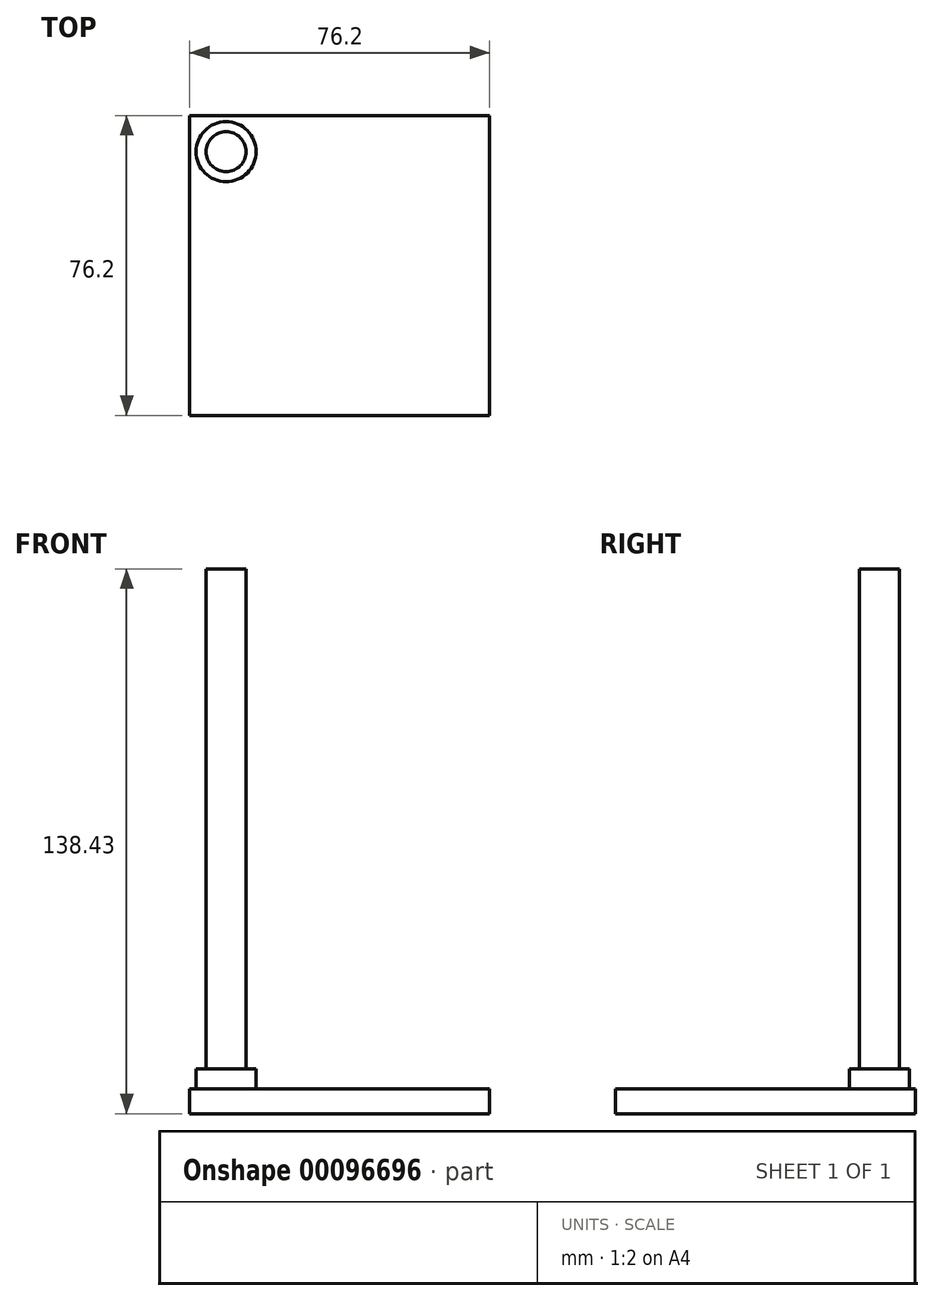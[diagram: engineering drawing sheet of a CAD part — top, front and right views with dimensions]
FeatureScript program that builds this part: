
annotation { "Feature Type Name" : "Feature", "Feature Type Description" : "" }
export const myFeature = defineFeature(function(context is Context, id is Id, definition is map)
    precondition{}
    {
        {
            var Q0;
            Q0=qCreatedBy(makeId("Top.planeOp"),FACE);
            var sketch = newSketch(context, id + "F0", { "sketchPlane" : qUnion([Q0])});
            skLineSegment(sketch, "E0.bottom", {"start": v(20.65, 3.83) * mm, "end": v(-55.55, 3.83) * mm});
            skLineSegment(sketch, "E0.top", {"start": v(20.65, -72.37) * mm, "end": v(-55.55, -72.37) * mm});
            skLineSegment(sketch, "E0.left", {"start": v(20.65, 3.83) * mm, "end": v(20.65, -72.37) * mm});
            skLineSegment(sketch, "E0.right", {"start": v(-55.55, 3.83) * mm, "end": v(-55.55, -72.37) * mm});
            skPoint(sketch, "E0.middle", {"position": v(-17.45, -34.27) * mm});
            skLineSegment(sketch, "E1", {"start": v(-55.55, 3.83) * mm, "end": v(-17.45, -34.27) * mm, "construction": true});
            skCircle(sketch, "E2", {"center": v(-46.33, -5.4) * mm, "radius": 5.08 * mm});
            skCircle(sketch, "E3", {"center": v(-46.33, -5.4) * mm, "radius": 7.62 * mm});
            skSolve(sketch);
        }
        {
            var Q0;
            Q0=makeQuery(id+"F0.imprint","IMPRINT",FACE,{"disambiguationData":[TD([[makeQuery(id+"F0.imprint","IMPRINT",EDGE,{"derivedFrom":sQuery(id+"F0.wireOp",EDGE,"E0.bottom")}),1.0]])]});
            var Q1;
            Q1=makeQuery(id+"F0.imprint","IMPRINT",FACE,{"disambiguationData":[TD([[makeQuery(id+"F0.imprint","IMPRINT",EDGE,{"derivedFrom":sQuery(id+"F0.wireOp",EDGE,"w2bagRfS-LO2H-fxX3-UejF-2K8wmvuM6gnf")}),1.0]])]});
            var Q2;
            Q2=makeQuery(id+"F0.imprint","IMPRINT",FACE,{"disambiguationData":[TD([[makeQuery(id+"F0.imprint","IMPRINT",EDGE,{"derivedFrom":sQuery(id+"F0.wireOp",EDGE,"E2")}),-1.0]])]});
            var Q3;
            Q3=makeQuery(id+"F0.imprint","IMPRINT",FACE,{"disambiguationData":[TD([[makeQuery(id+"F0.imprint","IMPRINT",EDGE,{"derivedFrom":sQuery(id+"F0.wireOp",EDGE,"E2")}),1.0]])]});
            extrude(context, id + "F1", {"entities" : qUnion([Q0, Q1, Q2, Q3]), "oppositeDirection" : true, "depth" : 6.35 * mm});
        }
        {
            var Q0;
            Q0=makeQuery(id+"F0.imprint","IMPRINT",FACE,{"disambiguationData":[TD([[makeQuery(id+"F0.imprint","IMPRINT",EDGE,{"derivedFrom":sQuery(id+"F0.wireOp",EDGE,"E2")}),1.0]])]});
            extrude(context, id + "F2", {"entities" : qUnion([Q0]), "operationType" : NewBodyOperationType.ADD, "depth" : 132.08 * mm});
        }
        {
            var Q0;
            Q0=makeQuery(id+"F0.imprint","IMPRINT",FACE,{"disambiguationData":[TD([[makeQuery(id+"F0.imprint","IMPRINT",EDGE,{"derivedFrom":sQuery(id+"F0.wireOp",EDGE,"E2")}),-1.0]])]});
            extrude(context, id + "F3", {"entities" : qUnion([Q0]), "operationType" : NewBodyOperationType.ADD, "depth" : 5.08 * mm});
        }
    });
